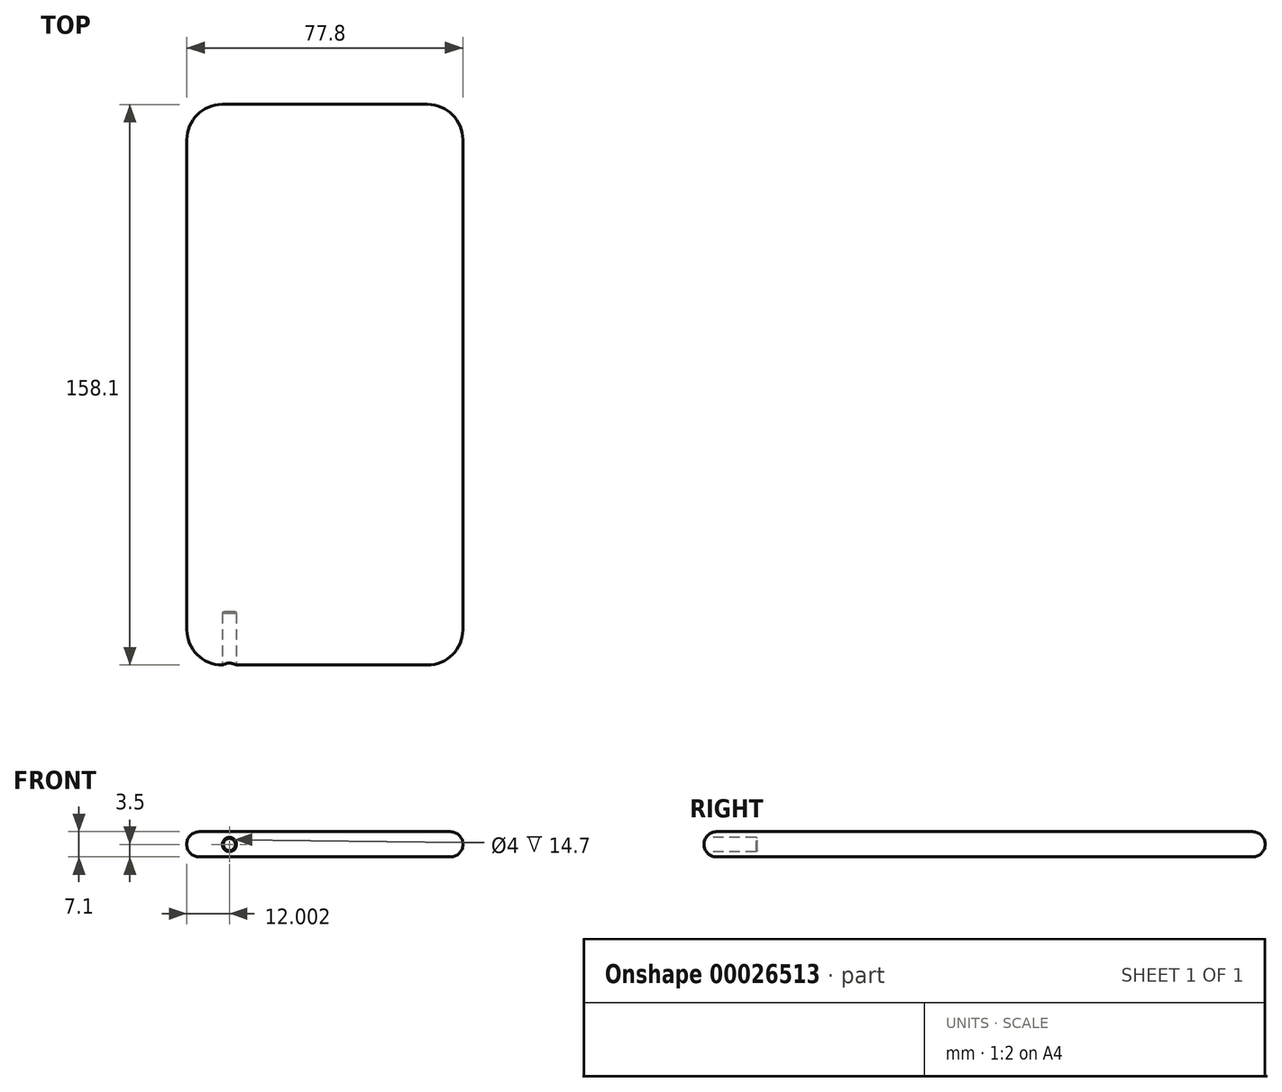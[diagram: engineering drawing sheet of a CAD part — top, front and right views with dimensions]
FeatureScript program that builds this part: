
annotation { "Feature Type Name" : "Feature", "Feature Type Description" : "" }
export const myFeature = defineFeature(function(context is Context, id is Id, definition is map)
    precondition{}
    {
        {
            var Q0;
            Q0=qCreatedBy(makeId("Top.planeOp"),FACE);
            var sketch = newSketch(context, id + "F0", { "sketchPlane" : qUnion([Q0])});
            skLineSegment(sketch, "E0.bottom", {"start": v(-34.26, 87.61) * mm, "end": v(43.54, 87.61) * mm});
            skLineSegment(sketch, "E0.top", {"start": v(-34.26, -70.49) * mm, "end": v(43.54, -70.49) * mm});
            skLineSegment(sketch, "E0.left", {"start": v(-34.26, 87.61) * mm, "end": v(-34.26, -70.49) * mm});
            skLineSegment(sketch, "E0.right", {"start": v(43.54, 87.61) * mm, "end": v(43.54, -70.49) * mm});
            skSolve(sketch);
        }
        {
            var Q0;
            Q0=makeQuery(id+"F0.imprint","IMPRINT",FACE,{"disambiguationData":[TD([[makeQuery(id+"F0.imprint","IMPRINT",EDGE,{"derivedFrom":sQuery(id+"F0.wireOp",EDGE,"E0.bottom")}),-1.0]])]});
            var sketch = newSketch(context, id + "F1", { "sketchPlane" : qUnion([Q0])});
            skSolve(sketch);
        }
        {
            var Q0;
            Q0 = qSketchRegion(id + "F1", true);
            var Q1;
            Q1=makeQuery(id+"F0.imprint","IMPRINT",FACE,{"disambiguationData":[TD([[makeQuery(id+"F0.imprint","IMPRINT",EDGE,{"derivedFrom":sQuery(id+"F0.wireOp",EDGE,"E0.bottom")}),-1.0]])]});
            extrude(context, id + "F2", {"entities" : qUnion([Q0, Q1]), "depth" : 7.1 * mm});
        }
        {
            var Q0;
            Q0=makeQuery(id+"F2.opExtrude","SWEPT_EDGE",EDGE,{"disambiguationData":[OSD([sQuery(id+"F0.wireOp",EDGE,"E0.top"),sQuery(id+"F0.wireOp",EDGE,"E0.right")])]});
            var Q1;
            Q1=makeQuery(id+"F2.opExtrude","SWEPT_EDGE",EDGE,{"disambiguationData":[OSD([sQuery(id+"F0.wireOp",EDGE,"E0.top"),sQuery(id+"F0.wireOp",EDGE,"E0.left")])]});
            var Q2;
            Q2=makeQuery(id+"F2.opExtrude","SWEPT_EDGE",EDGE,{"disambiguationData":[OSD([sQuery(id+"F0.wireOp",EDGE,"E0.bottom"),sQuery(id+"F0.wireOp",EDGE,"E0.right")])]});
            var Q3;
            Q3=makeQuery(id+"F2.opExtrude","SWEPT_EDGE",EDGE,{"disambiguationData":[OSD([sQuery(id+"F0.wireOp",EDGE,"E0.bottom"),sQuery(id+"F0.wireOp",EDGE,"E0.left")])]});
            fillet(context, id + "F3", {"entities" : qUnion([Q0, Q1, Q2, Q3]), "radius" : 10 * mm, "tangentPropagation" : true, "allowEdgeOverflow" : false});
        }
        {
            var Q0;
            Q0=makeQuery(id+"F2.opExtrude","CAP_FACE",FACE,{"disambiguationData":[OSD([sQuery(id+"F0.wireOp",EDGE,"E0.bottom"),sQuery(id+"F0.wireOp",EDGE,"E0.top"),sQuery(id+"F0.wireOp",EDGE,"E0.left"),sQuery(id+"F0.wireOp",EDGE,"E0.right")])],"isStart":false});
            var Q1;
            Q1=makeQuery(id+"F2.opExtrude","CAP_FACE",FACE,{"disambiguationData":[OSD([sQuery(id+"F0.wireOp",EDGE,"E0.bottom"),sQuery(id+"F0.wireOp",EDGE,"E0.top"),sQuery(id+"F0.wireOp",EDGE,"E0.left"),sQuery(id+"F0.wireOp",EDGE,"E0.right")])],"isStart":true});
            fillet(context, id + "F4", {"entities" : qUnion([Q0, Q1]), "radius" : 3.5 * mm, "tangentPropagation" : true, "allowEdgeOverflow" : false});
        }
        {
            var Q0;
            Q0=makeQuery(id+"F2.opExtrude","SWEPT_FACE",FACE,{"disambiguationData":[OSD([sQuery(id+"F0.wireOp",EDGE,"E0.top")])]});
            var sketch = newSketch(context, id + "F5", { "sketchPlane" : qUnion([Q0])});
            skCircle(sketch, "E1", {"center": v(-22.26, 3.5) * mm, "radius": 2 * mm});
            skSolve(sketch);
        }
        {
            var Q0;
            {var subQ0=sQuery(id+"F0.wireOp",EDGE,"E0.top");var subQ1=makeQuery(id+"F4.opFillet","BLEND_EDGE",EDGE,{"blendedFrom":[makeQuery(id+"F2.opExtrude","CAP_EDGE",EDGE,{"disambiguationData":[OSD([subQ0])],"isStart":false}),makeQuery(id+"F2.opExtrude","SWEPT_FACE",FACE,{"disambiguationData":[OSD([subQ0])]})],"blendedInto":[makeQuery(id+"F2.opExtrude","SWEPT_FACE",FACE,{"disambiguationData":[OSD([subQ0])]})]});var subQ2=sQuery(id+"F5.wireOp",EDGE,"E1");var subQ4=makeQuery(id+"F5.imprint","INTERSECT",VERTEX,{"disambiguationData":[OD(0.0)],"derivedFrom":[subQ1,subQ2]});Q0=makeQuery(id+"F5.imprint","IMPRINT",FACE,{"disambiguationData":[TD([[makeQuery(id+"F5.imprint","IMPRINT",EDGE,{"disambiguationData":[TD([[subQ4,-1.0]])],"derivedFrom":subQ2}),1.0]])]});}
            var Q1;
            {var subQ0=sQuery(id+"F0.wireOp",EDGE,"E0.top");var subQ1=makeQuery(id+"F2.opExtrude","SWEPT_FACE",FACE,{"disambiguationData":[OSD([subQ0])]});var subQ2=makeQuery(id+"F4.opFillet","BLEND_EDGE",EDGE,{"blendedFrom":[makeQuery(id+"F2.opExtrude","CAP_EDGE",EDGE,{"disambiguationData":[OSD([subQ0])],"isStart":true}),subQ1],"blendedInto":[subQ1]});var subQ3=sQuery(id+"F5.wireOp",EDGE,"E1");var subQ4=makeQuery(id+"F5.imprint","INTERSECT",VERTEX,{"derivedFrom":[subQ2,subQ3]});Q1=makeQuery(id+"F5.imprint","IMPRINT",FACE,{"disambiguationData":[TD([[makeQuery(id+"F5.imprint","IMPRINT",EDGE,{"disambiguationData":[TD([[subQ4,1.0]])],"derivedFrom":subQ3}),1.0]])]});}
            var Q2;
            {var subQ0=sQuery(id+"F0.wireOp",EDGE,"E0.top");var subQ1=makeQuery(id+"F2.opExtrude","SWEPT_FACE",FACE,{"disambiguationData":[OSD([subQ0])]});var subQ2=subQ1;var subQ3=makeQuery(id+"F4.opFillet","BLEND_EDGE",EDGE,{"blendedFrom":[makeQuery(id+"F2.opExtrude","CAP_EDGE",EDGE,{"disambiguationData":[OSD([subQ0])],"isStart":false}),subQ2],"blendedInto":[subQ2]});var subQ4=sQuery(id+"F5.wireOp",EDGE,"E1");var subQ6=makeQuery(id+"F5.imprint","INTERSECT",VERTEX,{"disambiguationData":[OD(0.0)],"derivedFrom":[subQ3,subQ4]});Q2=makeQuery(id+"F5.imprint","IMPRINT",FACE,{"disambiguationData":[TD([[makeQuery(id+"F5.imprint","IMPRINT",EDGE,{"disambiguationData":[TD([[subQ6,1.0]])],"derivedFrom":subQ4}),1.0]])]});}
            extrude(context, id + "F6", {"entities" : qUnion([Q0, Q1, Q2]), "operationType" : NewBodyOperationType.REMOVE, "oppositeDirection" : true, "depth" : 25 * mm});
        }
        {
            var Q0;
            Q0=makeQuery(id+"F6.boolean.opBoolean","COPY",FACE,{"derivedFrom":makeQuery(id+"F6.opExtrude","CAP_FACE",FACE,{"disambiguationData":[OSD([sQuery(id+"F5.wireOp",EDGE,"E1")])],"isStart":false})});
            extrude(context, id + "F7", {"entities" : qUnion([Q0]), "operationType" : NewBodyOperationType.ADD, "depth" : 10 * mm});
        }
        {
            var Q0;
            Q0=makeQuery(id+"F7.opExtrude","CAP_FACE",FACE,{"disambiguationData":[OSD([sQuery(id+"F5.wireOp",EDGE,"E1")])],"isStart":false});
            chamfer(context, id + "F8", {"entities" : qUnion([Q0]), "width" : 0.3 * mm, "tangentPropagation" : true});
        }
    });
